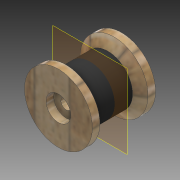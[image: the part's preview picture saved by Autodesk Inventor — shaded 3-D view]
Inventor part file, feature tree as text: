
AUTODESK INVENTOR PART (.ipt)
format: ipt  version: 2020 (Build 240168000, 168)  size: 147,968 bytes
history: native  units: mm
features: revolve x1, plane x1, sketch x1
ambient origin geometry x8: Origin, YZ Plane, XZ Plane, XY Plane, X Axis, Y Axis, Z Axis, Center Point
bodies: Solid1 (feature_tree)
feature tree (3):
  revolve  "Revolution1"  [1 undecoded]
  plane  "Work Plane1"
  sketch  "Sketch1"  dims[d0=58.0mm d1=20.0mm d5=12.225mm d7=10.0mm d8=35.0mm d9=12.225mm d10=10.0mm d12=90.0deg d14=8.5mm d15=102.45mm d16=77.45mm d17=12.5mm d18=35.0mm d19=40.0mm d20=35.0mm d21=12.225mm d22=10.0mm]
note: 1 required parameter value undecoded (feature->parameter linkage not recoverable at this tier; creation-order binding heuristic only, values carry confidence <= 0.55)
